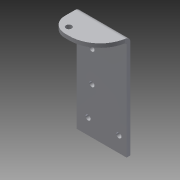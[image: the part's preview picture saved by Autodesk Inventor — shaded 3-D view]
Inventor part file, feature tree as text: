
AUTODESK INVENTOR PART (.ipt)
format: ipt  version: 2014 (Build 180170000, 170)  size: 164,864 bytes
history: native  units: in
note: dims shown in document units (in); Inventor stores cm internally (conversion verified against a paired STEP export)
features: sheet_metal_op x4, other x4, sketch x3, fillet x1
ambient origin geometry x8: Origin, YZ Plane, XZ Plane, XY Plane, X Axis, Y Axis, Z Axis, Center Point
bodies: Solid1 (feature_tree)
feature tree (12):
  sheet_metal_op  "Face1"
  sheet_metal_op  "Flange1"
  fillet  "Fillet2"  Radius=1.625in
  sketch  "Sketch1"  dims[d1=3.1875in]
  other  "Plate1"
  sketch  "Sketch2"  dims[d2=0.163in]
  other  "Plate2"
  sheet_metal_op  "Bend1"
  sheet_metal_op  "Corner1"
  sketch  "Sketch4"  dims[d4=0.7874in d6=1.0in d7=0.3937in d9=1.0in d11=0.125in d12=0.125in d13=0.0625in d14=0.25in d15=0.125in d16=1.0in d17=90.0deg d18=0.05in d19=0.5in d20=0.125in d21=0.125in d22=0.5in d28=0.187in d29=0.25in d31=0.125in d32=0.0in d34=0.375in d35=0.5in d36=0.25in d37=1.0in d38=0.5in d39=1.5in d40=0.7874in d42=1.0in d43=0.3937in d45=1.0in]
  other  "Cut2"
  other  "Definition1"
